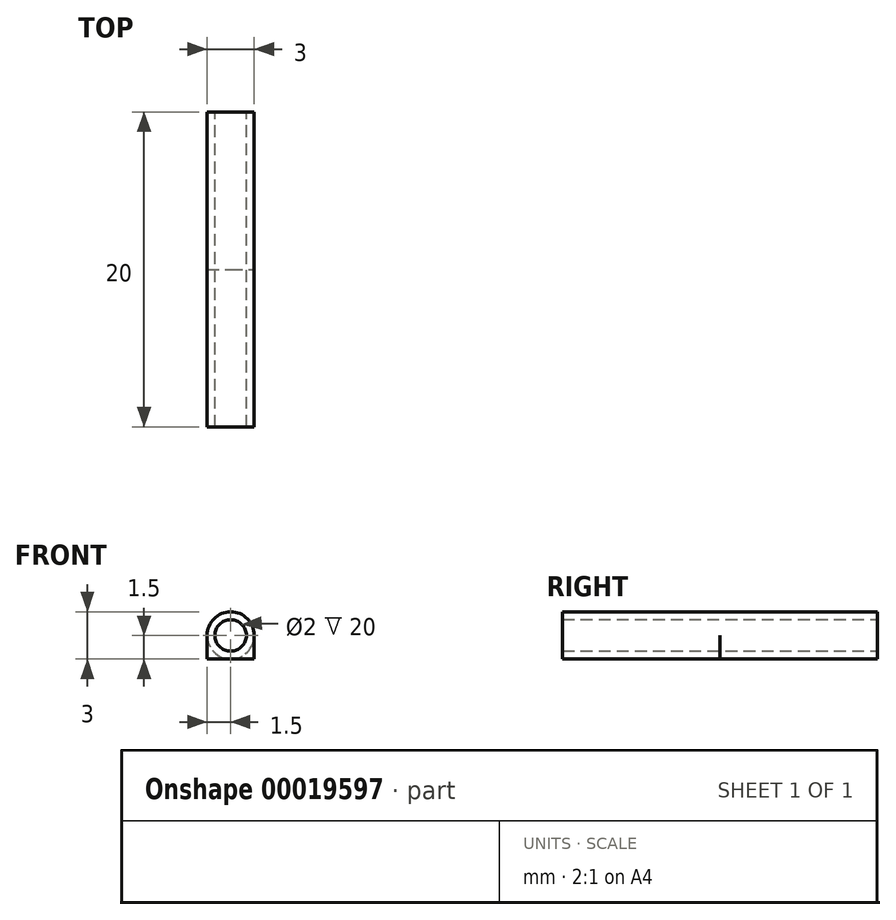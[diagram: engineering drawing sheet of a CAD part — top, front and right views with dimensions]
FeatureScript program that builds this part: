
annotation { "Feature Type Name" : "Feature", "Feature Type Description" : "" }
export const myFeature = defineFeature(function(context is Context, id is Id, definition is map)
    precondition{}
    {
        {
            var Q0;
            Q0=qCreatedBy(makeId("Front.planeOp"),FACE);
            var sketch = newSketch(context, id + "F0", { "sketchPlane" : qUnion([Q0])});
            skCircle(sketch, "E0", {"center": v(0, 0) * mm, "radius": 1 * mm});
            skCircle(sketch, "E1", {"center": v(0, 0) * mm, "radius": 1.5 * mm});
            skSolve(sketch);
        }
        {
            var Q0;
            Q0=qSketchRegion(id+"F0",true);
            extrude(context, id + "F1", {"entities" : qUnion([Q0]), "depth" : 20 * mm});
        }
        {
            var Q0;
            Q0=makeQuery(id+"F1.opExtrude","CAP_FACE",FACE,{"disambiguationData":[OSD([sQuery(id+"F0.wireOp",EDGE,"E0"),sQuery(id+"F0.wireOp",EDGE,"E1")])],"isStart":false});
            var sketch = newSketch(context, id + "F2", { "sketchPlane" : qUnion([Q0])});
            skLineSegment(sketch, "E2", {"start": v(-1.5, -1.5) * mm, "end": v(1.5, -1.5) * mm});
            skLineSegment(sketch, "E3", {"start": v(-1.5, 0) * mm, "end": v(-1.5, -1.5) * mm});
            skLineSegment(sketch, "E4", {"start": v(1.5, 0) * mm, "end": v(1.5, -1.5) * mm});
            skArc(sketch, "E5", {"start": v(-1.5, 0) * mm, "mid": v(0, -1.5) * mm, "end": v(1.5, 0) * mm});
            skSolve(sketch);
        }
        {
            var Q0;
            Q0=qSketchRegion(id+"F2",true);
            extrude(context, id + "F3", {"entities" : qUnion([Q0]), "operationType" : NewBodyOperationType.ADD, "oppositeDirection" : true, "depth" : 10 * mm});
        }
    });
